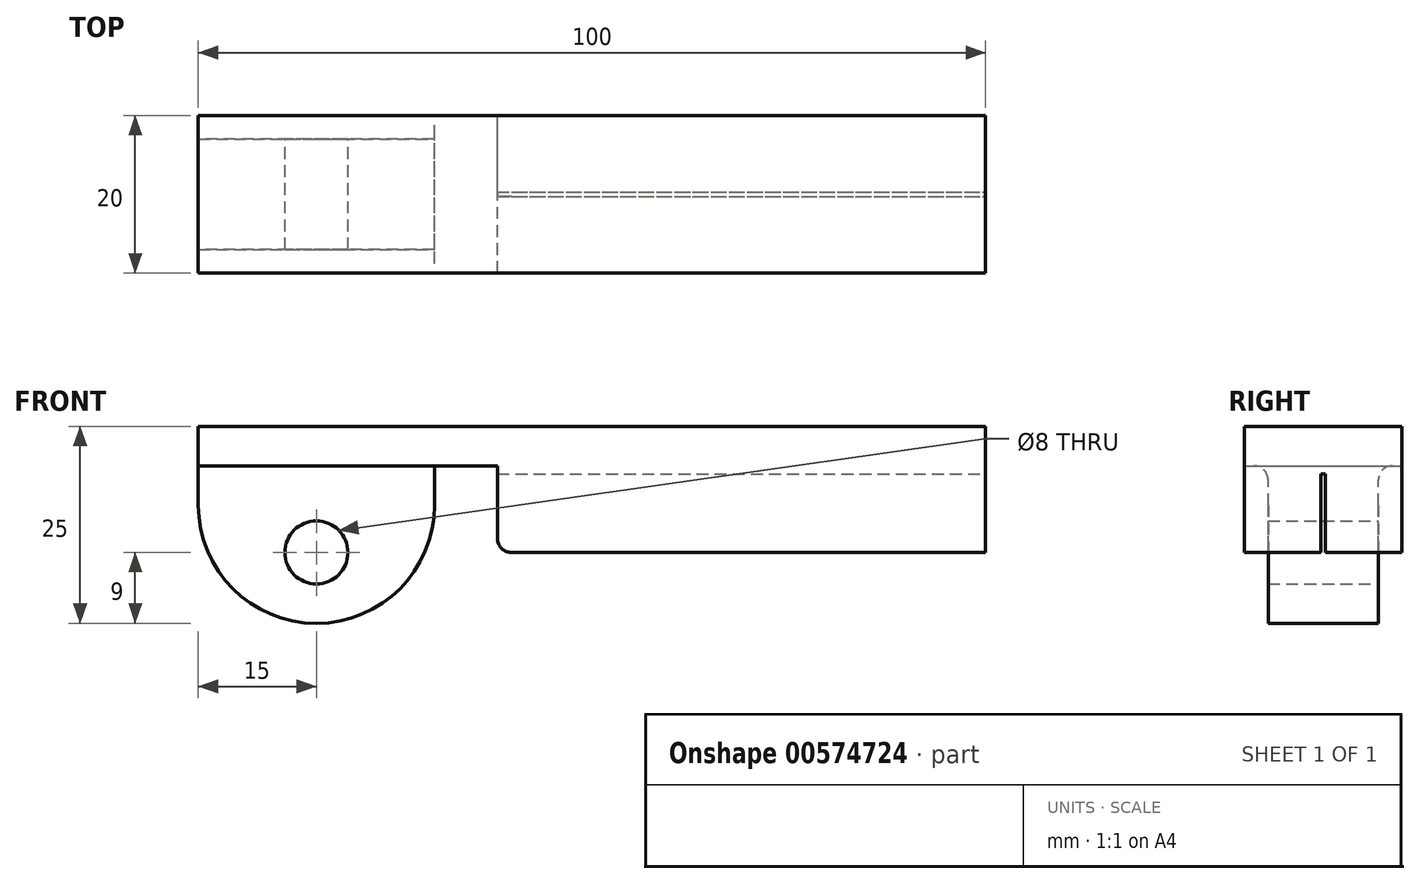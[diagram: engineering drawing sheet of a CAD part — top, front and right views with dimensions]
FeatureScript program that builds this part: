
annotation { "Feature Type Name" : "Feature", "Feature Type Description" : "" }
export const myFeature = defineFeature(function(context is Context, id is Id, definition is map)
    precondition{}
    {
        {
            var Q0;
            Q0=qCreatedBy(makeId("Front.planeOp"),FACE);
            var sketch = newSketch(context, id + "F0", { "sketchPlane" : qUnion([Q0])});
            skLineSegment(sketch, "E0", {"start": v(0, 25) * mm, "end": v(100, 25) * mm});
            skLineSegment(sketch, "E1", {"start": v(100, 25) * mm, "end": v(100, 9) * mm});
            skLineSegment(sketch, "E2", {"start": v(100, 9) * mm, "end": v(38, 9) * mm});
            skLineSegment(sketch, "E3", {"start": v(38, 9) * mm, "end": v(38, 20) * mm});
            skLineSegment(sketch, "E4", {"start": v(38, 20) * mm, "end": v(0, 20) * mm});
            skLineSegment(sketch, "E5", {"start": v(0, 20) * mm, "end": v(0, 25) * mm});
            skArc(sketch, "E6", {"start": v(0, 15) * mm, "mid": v(15, 0) * mm, "end": v(30, 15) * mm});
            skLineSegment(sketch, "E7", {"start": v(30, 15) * mm, "end": v(30, 20) * mm});
            skLineSegment(sketch, "E8", {"start": v(0, 15) * mm, "end": v(0, 20) * mm});
            skCircle(sketch, "E9", {"center": v(15, 9) * mm, "radius": 4 * mm});
            skSolve(sketch);
        }
        {
            var Q0;
            Q0=makeQuery(id+"F0.imprint","IMPRINT",FACE,{"disambiguationData":[TD([[makeQuery(id+"F0.imprint","IMPRINT",EDGE,{"derivedFrom":sQuery(id+"F0.wireOp",EDGE,"E0")}),-1.0]])]});
            extrude(context, id + "F1", {"entities" : qUnion([Q0]), "endBound" : BoundingType.SYMMETRIC, "depth" : 20 * mm, "offsetDistance" : 25 * mm});
        }
        {
            var Q0;
            Q0 = qSketchRegion(id + "F0", true);
            extrude(context, id + "F2", {"entities" : qUnion([Q0]), "operationType" : NewBodyOperationType.ADD, "endBound" : BoundingType.SYMMETRIC, "depth" : 14 * mm, "offsetDistance" : 25 * mm});
        }
        {
            var Q0;
            Q0=makeQuery(id+"F2.opExtrude","SWEPT_EDGE",EDGE,{"disambiguationData":[OSD([sQuery(id+"F0.wireOp",EDGE,"E4"),sQuery(id+"F0.wireOp",EDGE,"E7")])]});
            var Q1;
            {var subQ0=sQuery(id+"F0.wireOp",EDGE,"E4");Q1=makeQuery(id+"F2.boolean.opBoolean","INTERSECT",EDGE,{"derivedFrom":[makeQuery(id+"F1.opExtrude","SWEPT_FACE",FACE,{"disambiguationData":[OSD([subQ0])]}),makeQuery(id+"F2.opExtrude","CAP_FACE",FACE,{"disambiguationData":[OSD([sQuery(id+"F0.wireOp",EDGE,"E0"),sQuery(id+"F0.wireOp",EDGE,"E1"),sQuery(id+"F0.wireOp",EDGE,"E2"),sQuery(id+"F0.wireOp",EDGE,"E3"),subQ0,sQuery(id+"F0.wireOp",EDGE,"E5"),sQuery(id+"F0.wireOp",EDGE,"E6"),sQuery(id+"F0.wireOp",EDGE,"E7"),sQuery(id+"F0.wireOp",EDGE,"E8"),sQuery(id+"F0.wireOp",EDGE,"E9")])],"isStart":false})]});}
            var Q2;
            {var subQ0=sQuery(id+"F0.wireOp",EDGE,"E4");Q2=makeQuery(id+"F2.boolean.opBoolean","INTERSECT",EDGE,{"derivedFrom":[makeQuery(id+"F1.opExtrude","SWEPT_FACE",FACE,{"disambiguationData":[OSD([subQ0])]}),makeQuery(id+"F2.opExtrude","CAP_FACE",FACE,{"disambiguationData":[OSD([sQuery(id+"F0.wireOp",EDGE,"E0"),sQuery(id+"F0.wireOp",EDGE,"E1"),sQuery(id+"F0.wireOp",EDGE,"E2"),sQuery(id+"F0.wireOp",EDGE,"E3"),subQ0,sQuery(id+"F0.wireOp",EDGE,"E5"),sQuery(id+"F0.wireOp",EDGE,"E6"),sQuery(id+"F0.wireOp",EDGE,"E7"),sQuery(id+"F0.wireOp",EDGE,"E8"),sQuery(id+"F0.wireOp",EDGE,"E9")])],"isStart":true})]});}
            var Q3;
            Q3=makeQuery(id+"F1.opExtrude","SWEPT_EDGE",EDGE,{"disambiguationData":[OSD([sQuery(id+"F0.wireOp",EDGE,"E2"),sQuery(id+"F0.wireOp",EDGE,"E3")])]});
            fillet(context, id + "F3", {"entities" : qUnion([Q0, Q1, Q2, Q3]), "radius" : 1.8 * mm, "tangentPropagation" : true, "allowEdgeOverflow" : false});
        }
        {
            var Q0;
            Q0=qCreatedBy(makeId("Right.planeOp"),FACE);
            cPlane(context, id + "F4", {"entities" : qUnion([Q0]), "cplaneType" : CPlaneType.OFFSET, "offset" : 100 * mm, "width" : 150 * mm, "height" : 150 * mm});
        }
        {
            var Q0;
            Q0=qCreatedBy(id+"F4.planeOp",FACE);
            var sketch = newSketch(context, id + "F5", { "sketchPlane" : qUnion([Q0])});
            skPoint(sketch, "E10.0", {"position": v(0, 9) * mm});
            skLineSegment(sketch, "E11", {"start": v(0, 9) * mm, "end": v(-0.3, 9) * mm});
            skLineSegment(sketch, "E12", {"start": v(-0.3, 9) * mm, "end": v(-0.3, 19) * mm});
            skLineSegment(sketch, "E13", {"start": v(-0.3, 19) * mm, "end": v(0.3, 19) * mm});
            skLineSegment(sketch, "E14", {"start": v(0.3, 19) * mm, "end": v(0.3, 9) * mm});
            skLineSegment(sketch, "E15", {"start": v(0.3, 9) * mm, "end": v(0, 9) * mm});
            skSolve(sketch);
        }
        {
            var Q0;
            Q0=makeQuery(id+"F5.imprint","IMPRINT",FACE,{"disambiguationData":[TD([[makeQuery(id+"F5.imprint","IMPRINT",EDGE,{"derivedFrom":sQuery(id+"F5.wireOp",EDGE,"E11")}),-1.0]])]});
            extrude(context, id + "F6", {"entities" : qUnion([Q0]), "operationType" : NewBodyOperationType.REMOVE, "oppositeDirection" : true, "depth" : 65 * mm, "offsetDistance" : 25 * mm});
        }
    });
